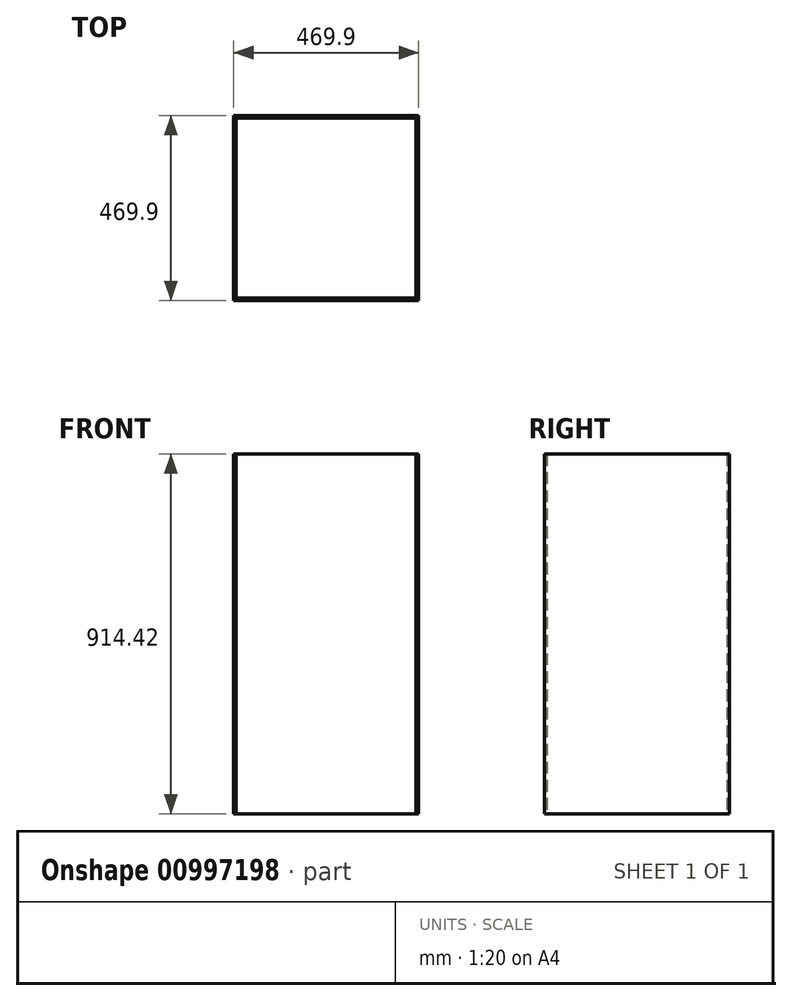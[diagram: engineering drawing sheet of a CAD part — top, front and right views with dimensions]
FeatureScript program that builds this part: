
annotation { "Feature Type Name" : "Feature", "Feature Type Description" : "" }
export const myFeature = defineFeature(function(context is Context, id is Id, definition is map)
    precondition{}
    {
        {
            var Q0;
            Q0=qCreatedBy(makeId("Top.planeOp"),FACE);
            var sketch = newSketch(context, id + "F0", { "sketchPlane" : qUnion([Q0])});
            skLineSegment(sketch, "E0.bottom", {"start": v(0, 0) * mm, "end": v(469.9, 0) * mm});
            skLineSegment(sketch, "E0.top", {"start": v(0, 469.9) * mm, "end": v(469.9, 469.9) * mm});
            skLineSegment(sketch, "E0.left", {"start": v(0, 0) * mm, "end": v(0, 469.9) * mm});
            skLineSegment(sketch, "E0.right", {"start": v(469.9, 0) * mm, "end": v(469.9, 469.9) * mm});
            skSolve(sketch);
        }
        {
            var Q0;
            Q0 = qSketchRegion(id + "F0", true);
            extrude(context, id + "F1", {"entities" : qUnion([Q0]), "depth" : 1 / 50.8 * mm, "offsetDistance" : 25.4 * mm});
        }
        {
            var Q0;
            Q0=makeQuery(id+"F1.opExtrude","CAP_FACE",FACE,{"disambiguationData":[OSD([sQuery(id+"F0.wireOp",EDGE,"E0.bottom"),sQuery(id+"F0.wireOp",EDGE,"E0.top"),sQuery(id+"F0.wireOp",EDGE,"E0.left"),sQuery(id+"F0.wireOp",EDGE,"E0.right")])],"isStart":false});
            var sketch = newSketch(context, id + "F2", { "sketchPlane" : qUnion([Q0])});
            skLineSegment(sketch, "E1.bottom", {"start": v(0, 0) * mm, "end": v(6.35, 0) * mm});
            skLineSegment(sketch, "E1.top", {"start": v(0, 469.9) * mm, "end": v(6.35, 469.9) * mm});
            skLineSegment(sketch, "E1.left", {"start": v(0, 0) * mm, "end": v(0, 469.9) * mm});
            skLineSegment(sketch, "E1.right", {"start": v(6.35, 0) * mm, "end": v(6.35, 469.9) * mm});
            skSolve(sketch);
        }
        {
            var Q0;
            Q0=makeQuery(id+"F1.opExtrude","CAP_FACE",FACE,{"disambiguationData":[OSD([sQuery(id+"F0.wireOp",EDGE,"E0.bottom"),sQuery(id+"F0.wireOp",EDGE,"E0.top"),sQuery(id+"F0.wireOp",EDGE,"E0.left"),sQuery(id+"F0.wireOp",EDGE,"E0.right")])],"isStart":false});
            var sketch = newSketch(context, id + "F3", { "sketchPlane" : qUnion([Q0])});
            skLineSegment(sketch, "E2.bottom", {"start": v(469.9, 0) * mm, "end": v(463.55, 0) * mm});
            skLineSegment(sketch, "E2.top", {"start": v(469.9, 469.9) * mm, "end": v(463.55, 469.9) * mm});
            skLineSegment(sketch, "E2.left", {"start": v(469.9, 0) * mm, "end": v(469.9, 469.9) * mm});
            skLineSegment(sketch, "E2.right", {"start": v(463.55, 0) * mm, "end": v(463.55, 469.9) * mm});
            skSolve(sketch);
        }
        {
            var Q0;
            Q0=makeQuery(id+"F1.opExtrude","CAP_FACE",FACE,{"disambiguationData":[OSD([sQuery(id+"F0.wireOp",EDGE,"E0.bottom"),sQuery(id+"F0.wireOp",EDGE,"E0.top"),sQuery(id+"F0.wireOp",EDGE,"E0.left"),sQuery(id+"F0.wireOp",EDGE,"E0.right")])],"isStart":false});
            var sketch = newSketch(context, id + "F4", { "sketchPlane" : qUnion([Q0])});
            skLineSegment(sketch, "E3.bottom", {"start": v(6.35, 469.9) * mm, "end": v(463.55, 469.9) * mm});
            skLineSegment(sketch, "E3.top", {"start": v(6.35, 463.55) * mm, "end": v(463.55, 463.55) * mm});
            skLineSegment(sketch, "E3.left", {"start": v(6.35, 469.9) * mm, "end": v(6.35, 463.55) * mm});
            skLineSegment(sketch, "E3.right", {"start": v(463.55, 469.9) * mm, "end": v(463.55, 463.55) * mm});
            skSolve(sketch);
        }
        {
            var Q0;
            Q0=makeQuery(id+"F1.opExtrude","CAP_FACE",FACE,{"disambiguationData":[OSD([sQuery(id+"F0.wireOp",EDGE,"E0.bottom"),sQuery(id+"F0.wireOp",EDGE,"E0.top"),sQuery(id+"F0.wireOp",EDGE,"E0.left"),sQuery(id+"F0.wireOp",EDGE,"E0.right")])],"isStart":false});
            var sketch = newSketch(context, id + "F5", { "sketchPlane" : qUnion([Q0])});
            skLineSegment(sketch, "E4.bottom", {"start": v(6.35, 0) * mm, "end": v(463.55, 0) * mm});
            skLineSegment(sketch, "E4.top", {"start": v(6.35, 6.35) * mm, "end": v(463.55, 6.35) * mm});
            skLineSegment(sketch, "E4.left", {"start": v(6.35, 0) * mm, "end": v(6.35, 6.35) * mm});
            skLineSegment(sketch, "E4.right", {"start": v(463.55, 0) * mm, "end": v(463.55, 6.35) * mm});
            skSolve(sketch);
        }
        {
            var Q0;
            Q0 = qSketchRegion(id + "F5", true);
            var Q1;
            Q1 = qSketchRegion(id + "F2", true);
            var Q2;
            Q2 = qSketchRegion(id + "F3", true);
            var Q3;
            Q3 = qSketchRegion(id + "F4", true);
            extrude(context, id + "F6", {"entities" : qUnion([Q0, Q1, Q2, Q3]), "depth" : 914.4 * mm, "offsetDistance" : 25.4 * mm});
        }
    });
